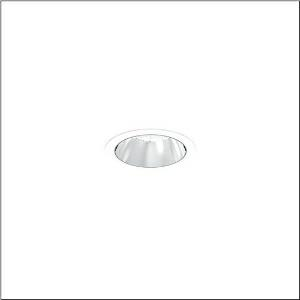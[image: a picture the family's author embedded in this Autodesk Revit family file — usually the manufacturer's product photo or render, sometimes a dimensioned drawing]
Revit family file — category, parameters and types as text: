
# Revit family: lunis_21_m_51db15ec91c
name_source: partatom
category: Lighting Fixtures
units: mm (PartAtom-declared; Revit-internal decimal feet)

## family parameters
Cut with Voids When Loaded = No
Host = Face
Light Source = No
Part Type = Normal
Room Calculation Point = No
Round Connector Dimension = Use Diameter
Shared = No

## types (1)
- --- (1 x LED, 3910 lm, 25.5 W, 6500K)
    Apparent Load = 26 VA
    CIE Flux Codes = 95 99 100 100 100
    Color Rendering = 80
    Color Temperature = 6500K
    Default Elevation = 1800 mm
    Description = Lunis 21,  M, downlight, light control with lens, of PMMA, anti glare with reflector, of PC, highly specular, light emission: direct distribution, LED rated luminous flux: 1.820lm, light colour: 830/840/865, with terminal, 5-pole, mains connection: 220..240V, AC/DC, 0/50..60Hz, housing, round, of diecast aluminium, traffic white (RAL 9016), diameter: 115mm, clamping range: 1..40mm, protection rating (complete): IP20, protection rating (on room side): IP54, insulation class (complete): insulation class II (safety insulation), certification: CE, impact resistance: IK03, packaging unit: 1 piece
    Height = 0 mm  [stored 0 ft]
    Lamp = 1 x LED
    Lamp Light Flux = 3910 lm
    Lamp Power = 25.5 W
    Lamp count = 1
    Length = 115 mm
    Luminous efficacy = 153 lm/W
    Manufacturer = Siteco
    ModVariant = No
    Model = 51DB15EC91C
    Mounting Place = Ceiling
    Mounting Type = Recessed
    Number of Poles = 1
    OnlyDefault = Yes
    Power Factor = 1
    Product Name = Lunis 21 M
    Product group = downlight
    ProductGroupID = 400
    Protection Class = Protection class II
    Protection Degree = IP 20
    RLX_Detail_Level = 1
    RLX_Emergency_Light_Flux = 0 lm
    RLX_Emergency_Type = 0
    RLX_Emergency_Type_DB = No
    RlxData = <blob elided: 15085 chars, md5=7ed085d9>
    Socket = socket
    Standby Power = 0 W
    System Light Flux = 3910 lm
    System Power = 26 W
    Type Comments = individual setting: colour temperature 6500K, luminous flux: 100 % | (ON | ON | OFF | OFF) | 700 mA
    Type Image = l_1290850.jpg
    URL = http://relux.com
    VarID = @adj_020570
    Voltage = 0 V
    Weight = 0.00 kg
    Width = 0 mm  [stored 0 ft]

note: [stored X ft] marks values corroborated as IEEE doubles in the binary element streams (Revit-internal decimal feet)

## geometry (parser evidence)
native form markers: Sweep x10
no freeform markers — native parametric forms only
